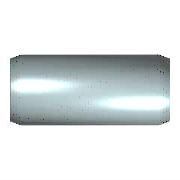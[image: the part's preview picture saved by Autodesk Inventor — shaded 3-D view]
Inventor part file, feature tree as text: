
AUTODESK INVENTOR PART (.ipt)
format: ipt  version: 2025.2 (Build 292293000, 293)  size: 113,664 bytes
history: native  units: mm (DEFAULTED — no unit token found)
features: chamfer x2, extrude x1
ambient origin geometry x8: Origin, YZ Plane, XZ Plane, XY Plane, X Axis, Y Axis, Z Axis, Center Point
bodies: Solid1 (feature_tree)
feature tree (3):
  extrude  "Körper"  Depth=3.0mm
  chamfer  "Fase1"  Distance=16.0mm
  chamfer  "Fase2"  [1 undecoded]
note: 1 required parameter value undecoded (feature->parameter linkage not recoverable at this tier; creation-order binding heuristic only, values carry confidence <= 0.55)
